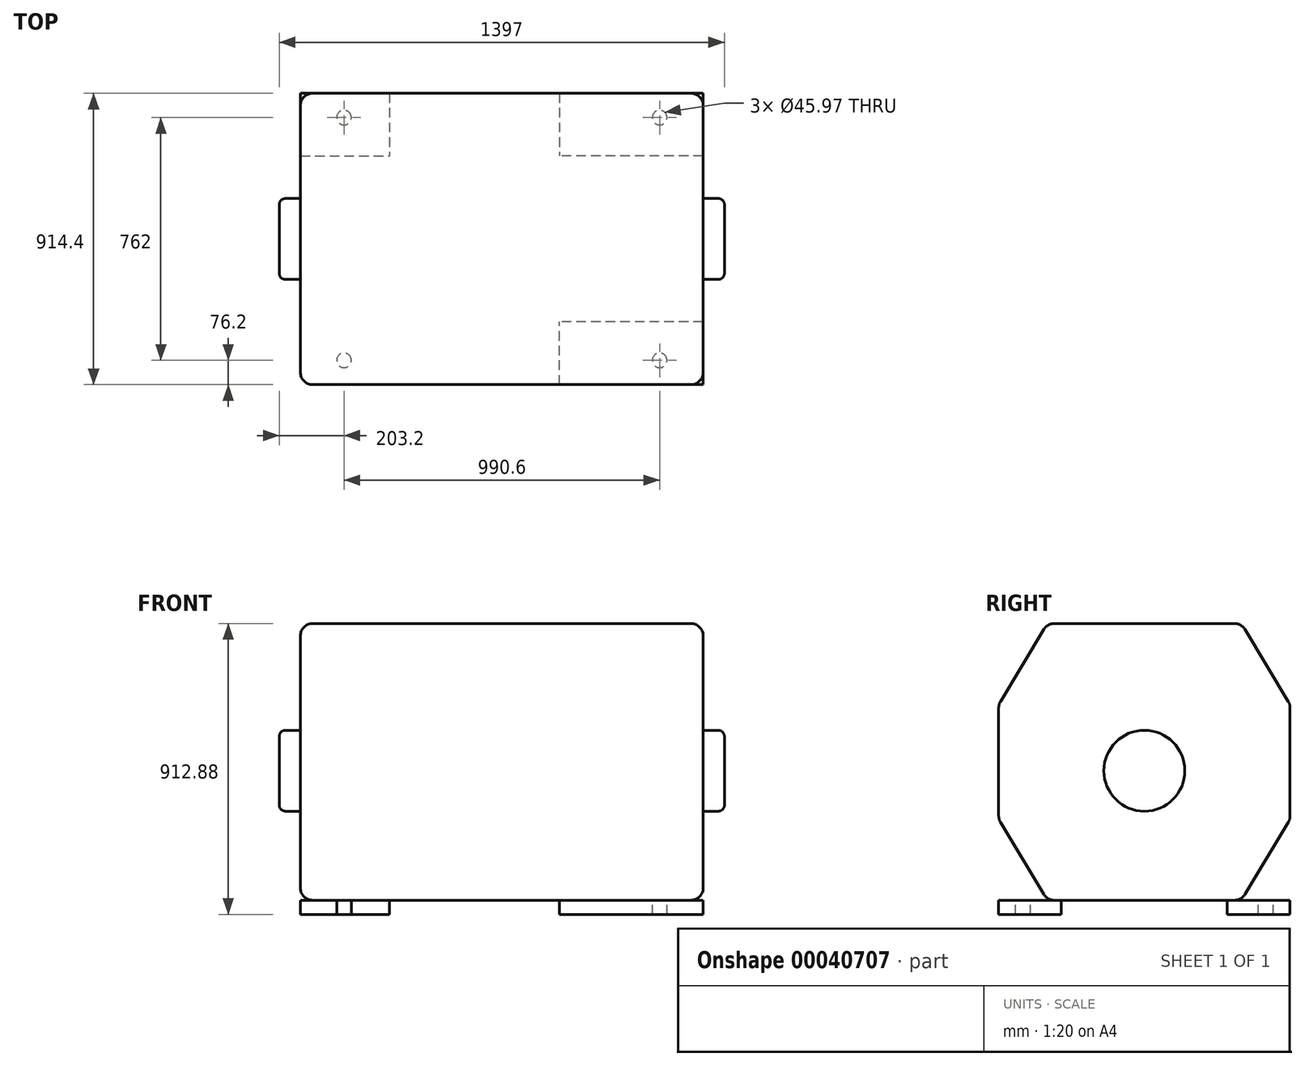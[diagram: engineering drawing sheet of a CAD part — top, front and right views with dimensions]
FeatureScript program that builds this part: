
annotation { "Feature Type Name" : "Feature", "Feature Type Description" : "" }
export const myFeature = defineFeature(function(context is Context, id is Id, definition is map)
    precondition{}
    {
        {
            var Q0;
            Q0=qCreatedBy(makeId("Top.planeOp"),FACE);
            var sketch = newSketch(context, id + "F0", { "sketchPlane" : qUnion([Q0])});
            skLineSegment(sketch, "E0.rect.bottom", {"start": v(-631.83, 457.2) * mm, "end": v(631.83, 457.2) * mm, "construction": true});
            skLineSegment(sketch, "E0.rect.top", {"start": v(-631.83, -457.2) * mm, "end": v(631.83, -457.2) * mm, "construction": true});
            skLineSegment(sketch, "E0.rect.left", {"start": v(-631.82, 457.2) * mm, "end": v(-631.83, -457.2) * mm, "construction": true});
            skLineSegment(sketch, "E0.rect.right", {"start": v(631.83, 457.2) * mm, "end": v(631.83, -457.2) * mm, "construction": true});
            skPoint(sketch, "E0.rect.middle", {"position": v(0, 0) * mm});
            skLineSegment(sketch, "E1.bottom", {"start": v(-631.83, 457.2) * mm, "end": v(-352.43, 457.2) * mm});
            skLineSegment(sketch, "E1.top", {"start": v(-631.83, 260.35) * mm, "end": v(-352.43, 260.35) * mm});
            skLineSegment(sketch, "E1.left", {"start": v(-631.83, 457.2) * mm, "end": v(-631.83, 260.35) * mm});
            skLineSegment(sketch, "E1.right", {"start": v(-352.43, 457.2) * mm, "end": v(-352.43, 260.35) * mm});
            skLineSegment(sketch, "E2.bottom", {"start": v(631.83, 457.2) * mm, "end": v(180.98, 457.2) * mm});
            skLineSegment(sketch, "E2.top", {"start": v(631.83, 260.35) * mm, "end": v(180.98, 260.35) * mm});
            skLineSegment(sketch, "E2.left", {"start": v(631.83, 457.2) * mm, "end": v(631.83, 260.35) * mm});
            skLineSegment(sketch, "E2.right", {"start": v(180.98, 457.2) * mm, "end": v(180.98, 260.35) * mm});
            skLineSegment(sketch, "E3", {"start": v(0, 476.86) * mm, "end": v(0, -472.8) * mm, "construction": true});
            skLineSegment(sketch, "E4", {"start": v(-689.14, 0) * mm, "end": v(696.03, 0) * mm, "construction": true});
            skPoint(sketch, "E4.endSnap0", {"position": v(631.83, 0) * mm});
            skLineSegment(sketch, "E5.0", {"start": v(-495.3, 476.86) * mm, "end": v(-495.3, -472.8) * mm, "construction": true});
            skLineSegment(sketch, "E6.0", {"start": v(-689.14, 381) * mm, "end": v(696.03, 381) * mm, "construction": true});
            skCircle(sketch, "E7", {"center": v(-495.3, 381) * mm, "radius": 22.99 * mm});
            skCircle(sketch, "E8.MirrorC", {"center": v(495.3, 381) * mm, "radius": 22.99 * mm});
            skCircle(sketch, "E9.MirrorC", {"center": v(-495.3, -381) * mm, "radius": 22.99 * mm});
            skLineSegment(sketch, "E10.MirrorCS", {"start": v(-631.83, -457.2) * mm, "end": v(-631.83, -260.35) * mm});
            skLineSegment(sketch, "E11.MirrorCS", {"start": v(-631.83, -260.35) * mm, "end": v(-352.43, -260.35) * mm});
            skLineSegment(sketch, "E12.MirrorCS", {"start": v(-352.43, -457.2) * mm, "end": v(-352.43, -260.35) * mm});
            skLineSegment(sketch, "E13.MirrorCS", {"start": v(-631.83, -457.2) * mm, "end": v(-352.43, -457.2) * mm});
            skLineSegment(sketch, "E14.MirrorCS", {"start": v(631.83, -457.2) * mm, "end": v(180.98, -457.2) * mm});
            skLineSegment(sketch, "E15.MirrorCS", {"start": v(631.83, -260.35) * mm, "end": v(180.98, -260.35) * mm});
            skLineSegment(sketch, "E16.MirrorCS", {"start": v(180.98, -457.2) * mm, "end": v(180.98, -260.35) * mm});
            skLineSegment(sketch, "E17.MirrorCS", {"start": v(631.83, -457.2) * mm, "end": v(631.83, -260.35) * mm});
            skLineSegment(sketch, "E18.MirrorCS", {"start": v(-631.83, -457.2) * mm, "end": v(631.83, -457.2) * mm});
            skLineSegment(sketch, "E19.MirrorCS", {"start": v(-689.14, -381) * mm, "end": v(696.03, -381) * mm, "construction": true});
            skCircle(sketch, "E20.MirrorC", {"center": v(495.3, -381) * mm, "radius": 22.99 * mm});
            skSolve(sketch);
        }
        {
            var Q0;
            Q0=makeQuery(id+"F0.imprint","IMPRINT",FACE,{"disambiguationData":[TD([[makeQuery(id+"F0.imprint","IMPRINT",EDGE,{"derivedFrom":sQuery(id+"F0.wireOp",EDGE,"E1.bottom")}),-1.0]])]});
            var Q1;
            Q1=makeQuery(id+"F0.imprint","IMPRINT",FACE,{"disambiguationData":[TD([[makeQuery(id+"F0.imprint","IMPRINT",EDGE,{"derivedFrom":sQuery(id+"F0.wireOp",EDGE,"E2.bottom")}),1.0]])]});
            var Q2;
            Q2=makeQuery(id+"F0.imprint","IMPRINT",FACE,{"disambiguationData":[TD([[makeQuery(id+"F0.imprint","IMPRINT",EDGE,{"derivedFrom":sQuery(id+"F0.wireOp",EDGE,"E15.MirrorCS")}),1.0]])]});
            var Q3;
            Q3=makeQuery(id+"F0.imprint","IMPRINT",FACE,{"disambiguationData":[TD([[makeQuery(id+"F0.imprint","IMPRINT",EDGE,{"derivedFrom":sQuery(id+"F0.wireOp",EDGE,"E9.MirrorC")}),1.0]])]});
            extrude(context, id + "F1", {"entities" : qUnion([Q0, Q1, Q2, Q3]), "oppositeDirection" : true, "depth" : 44.45 * mm});
        }
        {
            var Q0;
            Q0=qCreatedBy(makeId("Top.planeOp"),FACE);
            var sketch = newSketch(context, id + "F2", { "sketchPlane" : qUnion([Q0])});
            skLineSegment(sketch, "E21.0", {"start": v(-631.83, 457.2) * mm, "end": v(-352.43, 457.2) * mm, "construction": true});
            skLineSegment(sketch, "E22.0", {"start": v(180.98, -457.2) * mm, "end": v(631.83, -457.2) * mm, "construction": true});
            skLineSegment(sketch, "E23.bottom", {"start": v(-631.83, 457.2) * mm, "end": v(631.83, 457.2) * mm});
            skLineSegment(sketch, "E23.top", {"start": v(-631.83, -457.2) * mm, "end": v(631.83, -457.2) * mm});
            skLineSegment(sketch, "E23.left", {"start": v(-631.83, 457.2) * mm, "end": v(-631.83, -457.2) * mm});
            skLineSegment(sketch, "E23.right", {"start": v(631.83, 457.2) * mm, "end": v(631.83, -457.2) * mm});
            skSolve(sketch);
        }
        {
            var Q0;
            Q0=makeQuery(id+"F2.imprint","IMPRINT",FACE,{"disambiguationData":[TD([[makeQuery(id+"F2.imprint","IMPRINT",EDGE,{"derivedFrom":sQuery(id+"F2.wireOp",EDGE,"E23.bottom")}),-1.0]])]});
            extrude(context, id + "F3", {"entities" : qUnion([Q0]), "depth" : 868.43 * mm});
        }
        {
            var Q0;
            Q0=makeQuery(id+"F3.opExtrude","CAP_EDGE",EDGE,{"disambiguationData":[OSD([sQuery(id+"F2.wireOp",EDGE,"E23.top")])],"isStart":false});
            var Q1;
            Q1=makeQuery(id+"F3.opExtrude","CAP_EDGE",EDGE,{"disambiguationData":[OSD([sQuery(id+"F2.wireOp",EDGE,"E23.top")])],"isStart":true});
            var Q2;
            Q2=makeQuery(id+"F3.opExtrude","CAP_EDGE",EDGE,{"disambiguationData":[OSD([sQuery(id+"F2.wireOp",EDGE,"E23.bottom")])],"isStart":false});
            var Q3;
            Q3=makeQuery(id+"F3.opExtrude","CAP_EDGE",EDGE,{"disambiguationData":[OSD([sQuery(id+"F2.wireOp",EDGE,"E23.bottom")])],"isStart":true});
            chamfer(context, id + "F4", {"entities" : qUnion([Q0, Q1, Q2, Q3]), "chamferType" : ChamferType.TWO_OFFSETS, "width1" : 152.4 * mm, "oppositeDirection" : false, "width2" : 254 * mm, "tangentPropagation" : true});
        }
        {
            var Q0;
            Q0=makeQuery(id+"F3.opExtrude","SWEPT_FACE",FACE,{"disambiguationData":[OSD([sQuery(id+"F2.wireOp",EDGE,"E23.left")])]});
            var Q1;
            Q1=makeQuery(id+"F3.opExtrude","SWEPT_FACE",FACE,{"disambiguationData":[OSD([sQuery(id+"F2.wireOp",EDGE,"E23.right")])]});
            var Q2;
            {var subQ0=sQuery(id+"F2.wireOp",EDGE,"E23.bottom");Q2=makeQuery(id+"F4.opChamfer","BLEND_EDGE",EDGE,{"blendedFrom":[makeQuery(id+"F3.opExtrude","CAP_EDGE",EDGE,{"disambiguationData":[OSD([subQ0])],"isStart":true}),makeQuery(id+"F3.opExtrude","CAP_FACE",FACE,{"disambiguationData":[OSD([subQ0,sQuery(id+"F2.wireOp",EDGE,"E23.top"),sQuery(id+"F2.wireOp",EDGE,"E23.left"),sQuery(id+"F2.wireOp",EDGE,"E23.right")])],"isStart":true})],"blendedInto":[makeQuery(id+"F3.opExtrude","CAP_FACE",FACE,{"disambiguationData":[OSD([subQ0,sQuery(id+"F2.wireOp",EDGE,"E23.top"),sQuery(id+"F2.wireOp",EDGE,"E23.left"),sQuery(id+"F2.wireOp",EDGE,"E23.right")])],"isStart":true})]});}
            var Q3;
            {var subQ0=sQuery(id+"F2.wireOp",EDGE,"E23.bottom");Q3=makeQuery(id+"F4.opChamfer","BLEND_EDGE",EDGE,{"blendedFrom":[makeQuery(id+"F3.opExtrude","CAP_EDGE",EDGE,{"disambiguationData":[OSD([subQ0])],"isStart":true}),makeQuery(id+"F3.opExtrude","SWEPT_FACE",FACE,{"disambiguationData":[OSD([subQ0])]})],"blendedInto":[makeQuery(id+"F3.opExtrude","SWEPT_FACE",FACE,{"disambiguationData":[OSD([subQ0])]})]});}
            var Q4;
            Q4=makeQuery(id+"F3.opExtrude","SWEPT_FACE",FACE,{"disambiguationData":[OSD([sQuery(id+"F2.wireOp",EDGE,"E23.bottom")])]});
            var Q5;
            {var subQ0=sQuery(id+"F2.wireOp",EDGE,"E23.bottom");Q5=makeQuery(id+"F4.opChamfer","BLEND_FACE",FACE,{"disambiguationData":[OSD([subQ0]),TDD([makeQuery(id+"F3.opExtrude","CAP_EDGE",EDGE,{"disambiguationData":[OSD([subQ0])],"isStart":false})])]});}
            var Q6;
            Q6=makeQuery(id+"F3.opExtrude","CAP_FACE",FACE,{"disambiguationData":[OSD([sQuery(id+"F2.wireOp",EDGE,"E23.bottom"),sQuery(id+"F2.wireOp",EDGE,"E23.top"),sQuery(id+"F2.wireOp",EDGE,"E23.left"),sQuery(id+"F2.wireOp",EDGE,"E23.right")])],"isStart":false});
            var Q7;
            {var subQ0=sQuery(id+"F2.wireOp",EDGE,"E23.top");Q7=makeQuery(id+"F4.opChamfer","BLEND_FACE",FACE,{"disambiguationData":[OSD([subQ0]),TDD([makeQuery(id+"F3.opExtrude","CAP_EDGE",EDGE,{"disambiguationData":[OSD([subQ0])],"isStart":false})])]});}
            var Q8;
            Q8=makeQuery(id+"F3.opExtrude","SWEPT_FACE",FACE,{"disambiguationData":[OSD([sQuery(id+"F2.wireOp",EDGE,"E23.top")])]});
            var Q9;
            {var subQ0=sQuery(id+"F2.wireOp",EDGE,"E23.top");Q9=makeQuery(id+"F4.opChamfer","BLEND_FACE",FACE,{"disambiguationData":[OSD([subQ0]),TDD([makeQuery(id+"F3.opExtrude","CAP_EDGE",EDGE,{"disambiguationData":[OSD([subQ0])],"isStart":true})])]});}
            fillet(context, id + "F5", {"entities" : qUnion([Q0, Q1, Q2, Q3, Q4, Q5, Q6, Q7, Q8, Q9]), "radius" : 38.1 * mm, "tangentPropagation" : true, "allowEdgeOverflow" : false});
        }
        {
            var Q0;
            Q0=makeQuery(id+"F3.opExtrude","SWEPT_FACE",FACE,{"disambiguationData":[OSD([sQuery(id+"F2.wireOp",EDGE,"E23.right")])]});
            var sketch = newSketch(context, id + "F6", { "sketchPlane" : qUnion([Q0])});
            skLineSegment(sketch, "E24.0", {"start": v(-457.2, -44.45) * mm, "end": v(-260.35, -44.45) * mm, "construction": true});
            skLineSegment(sketch, "E25", {"start": v(0, 0) * mm, "end": v(0, 978.78) * mm, "construction": true});
            skLineSegment(sketch, "E26.0", {"start": v(-457.2, 406.4) * mm, "end": v(0, 406.4) * mm, "construction": true});
            skCircle(sketch, "E27", {"center": v(0, 406.4) * mm, "radius": 127 * mm});
            skSolve(sketch);
        }
        {
            var Q0;
            Q0 = qSketchRegion(id + "F6", true);
            extrude(context, id + "F7", {"entities" : qUnion([Q0]), "depth" : 66.67 * mm});
        }
        {
            var Q0;
            Q0=makeQuery(id+"F7.opExtrude","SWEPT_BODY",BODY,{"disambiguationData":[OSD([sQuery(id+"F6.wireOp",EDGE,"E27")])]});
            var Q1;
            Q1=qCreatedBy(makeId("Right.planeOp"),FACE);
            mirror(context, id + "F8", {"operationType" : NewBodyOperationType.ADD, "entities" : qUnion([Q0]), "mirrorPlane" : qUnion([Q1])});
        }
        {
            var Q0;
            Q0=makeQuery(id+"F7.opExtrude","CAP_EDGE",EDGE,{"disambiguationData":[OSD([sQuery(id+"F6.wireOp",EDGE,"E27")])],"isStart":true});
            var Q1;
            Q1=makeQuery(id+"F7.opExtrude","CAP_EDGE",EDGE,{"disambiguationData":[OSD([sQuery(id+"F6.wireOp",EDGE,"E27")])],"isStart":false});
            var Q2;
            Q2=makeQuery(id+"F8.opPattern","COPY",EDGE,{"derivedFrom":makeQuery(id+"F7.opExtrude","CAP_EDGE",EDGE,{"disambiguationData":[OSD([sQuery(id+"F6.wireOp",EDGE,"E27")])],"isStart":false}),"instanceName":"1"});
            var Q3;
            Q3=makeQuery(id+"F8.opPattern","COPY",EDGE,{"derivedFrom":makeQuery(id+"F7.opExtrude","CAP_EDGE",EDGE,{"disambiguationData":[OSD([sQuery(id+"F6.wireOp",EDGE,"E27")])],"isStart":true}),"instanceName":"1"});
            fillet(context, id + "F9", {"entities" : qUnion([Q0, Q1, Q2, Q3]), "radius" : 19.05 * mm, "tangentPropagation" : true, "allowEdgeOverflow" : false});
        }
        {
            var Q0;
            Q0=makeQuery(id+"F7.opExtrude","CAP_FACE",FACE,{"disambiguationData":[OSD([sQuery(id+"F6.wireOp",EDGE,"E27")])],"isStart":false});
            var sketch = newSketch(context, id + "F10", { "sketchPlane" : qUnion([Q0])});
            skCircle(sketch, "E28.0.0", {"center": v(0, 406.4) * mm, "radius": 107.95 * mm, "construction": true});
            skSolve(sketch);
        }
        {
            var Q0;
            Q0=sQuery(id+"F10.wireOp",VERTEX,"E28.0.0.center");
            var Q1;
            Q1=makeQuery(id+"F1.opExtrude","SWEPT_BODY",BODY,{"disambiguationData":[OSD([sQuery(id+"F0.wireOp",EDGE,"E9.MirrorC"),sQuery(id+"F0.wireOp",EDGE,"E10.MirrorCS"),sQuery(id+"F0.wireOp",EDGE,"E11.MirrorCS"),sQuery(id+"F0.wireOp",EDGE,"E12.MirrorCS"),sQuery(id+"F0.wireOp",EDGE,"E18.MirrorCS")])]});
            hole(context, id + "F11", {"style" : HoleStyle.SIMPLE, "holeDiameter" : 127 * mm, "endStyle" : HoleEndStyle.THROUGH, "locations" : qUnion([Q0]), "scope" : qUnion([Q1])});
        }
    });
